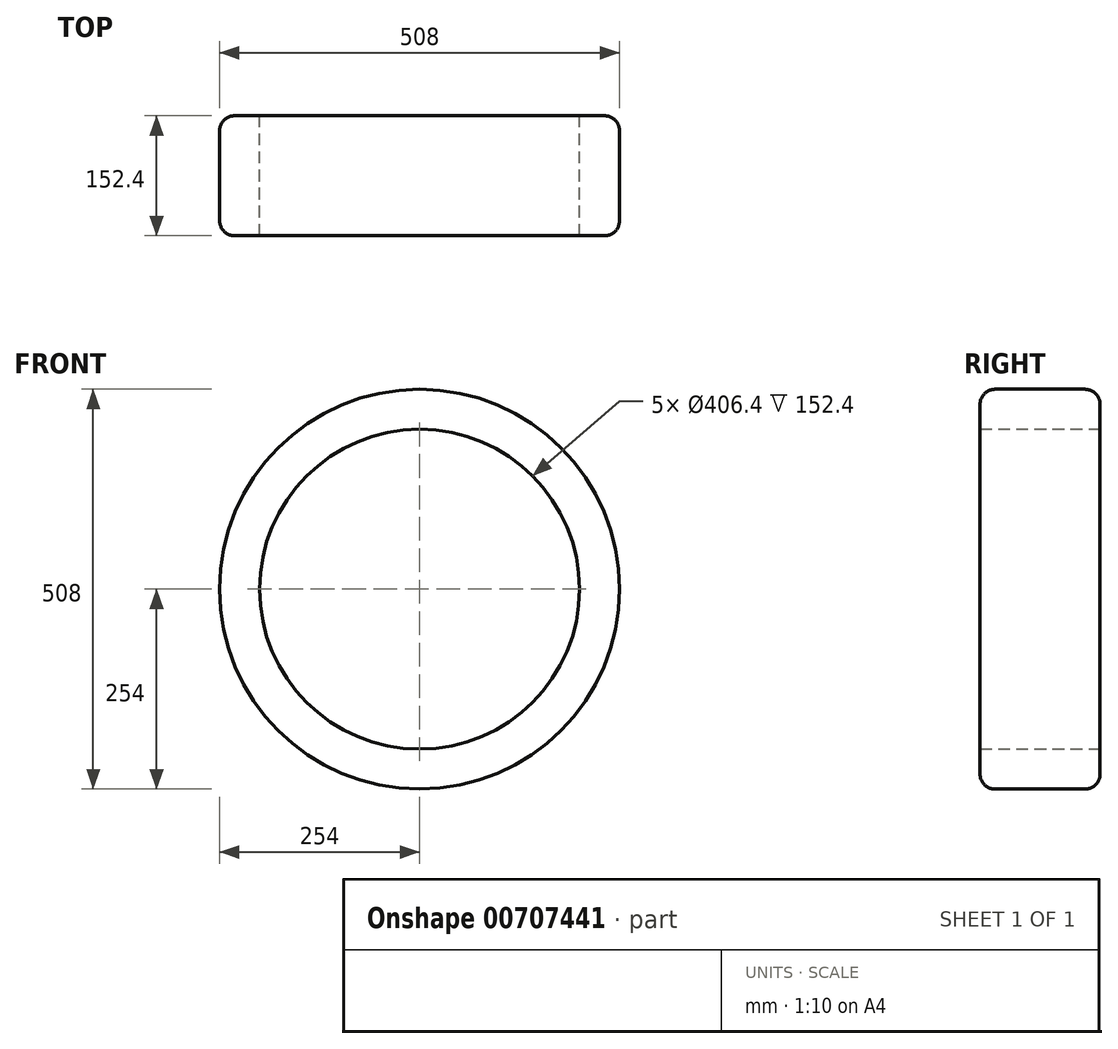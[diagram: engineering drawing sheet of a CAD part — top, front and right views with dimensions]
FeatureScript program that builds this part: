
annotation { "Feature Type Name" : "Feature", "Feature Type Description" : "" }
export const myFeature = defineFeature(function(context is Context, id is Id, definition is map)
    precondition{}
    {
        {
            var Q0;
            Q0=qCreatedBy(makeId("Front.planeOp"),FACE);
            var sketch = newSketch(context, id + "F0", { "sketchPlane" : qUnion([Q0])});
            skCircle(sketch, "E0", {"center": v(0, 0) * mm, "radius": 254 * mm});
            skLineSegment(sketch, "E1", {"start": v(320.36, 0) * mm, "end": v(-315.23, 0) * mm, "construction": true});
            skCircle(sketch, "E2.0", {"center": v(0, 0) * mm, "radius": 203.2 * mm});
            skSolve(sketch);
        }
        {
            var Q0;
            Q0=qCreatedBy(makeId("Top.planeOp"),FACE);
            var sketch = newSketch(context, id + "F1", { "sketchPlane" : qUnion([Q0])});
            skLineSegment(sketch, "E3", {"start": v(0, 100.46) * mm, "end": v(0, -121.76) * mm, "construction": true});
            skSolve(sketch);
        }
        {
            var Q0;
            Q0=makeQuery(id+"F0.imprint","IMPRINT",FACE,{"disambiguationData":[TD([[makeQuery(id+"F0.imprint","IMPRINT",EDGE,{"derivedFrom":sQuery(id+"F0.wireOp",EDGE,"E0")}),1.0]])]});
            extrude(context, id + "F2", {"entities" : qUnion([Q0]), "depth" : 76.2 * mm, "offsetDistance" : 25.4 * mm, "hasSecondDirection" : true, "secondDirectionOppositeDirection" : true, "secondDirectionDepth" : 76.2 * mm});
        }
        {
            var Q0;
            Q0=makeQuery(id+"F2.opExtrude","CAP_EDGE",EDGE,{"disambiguationData":[OSD([sQuery(id+"F0.wireOp",EDGE,"E0")])],"isStart":true});
            var Q1;
            Q1=makeQuery(id+"F2.opExtrude","CAP_EDGE",EDGE,{"disambiguationData":[OSD([sQuery(id+"F0.wireOp",EDGE,"E0")])],"isStart":false});
            fillet(context, id + "F3", {"entities" : qUnion([Q0, Q1]), "radius" : 19.05 * mm, "tangentPropagation" : true, "allowEdgeOverflow" : false});
        }
        {
            var Q0;
            Q0=sQuery(id+"F0.wireOp",EDGE,"E1");
            cPlane(context, id + "F4", {"entities" : qUnion([Q0]), "cplaneType" : CPlaneType.LINE_ANGLE, "offset" : 25.4 * mm, "angle" : 90 * degree, "width" : 152.4 * mm, "height" : 152.4 * mm});
        }
        {
            var Q0;
            Q0=qCreatedBy(id+"F4.planeOp",FACE);
            var sketch = newSketch(context, id + "F5", { "sketchPlane" : qUnion([Q0])});
            skLineSegment(sketch, "E4", {"start": v(234.95, 76.2) * mm, "end": v(234.95, -76.2) * mm});
            skArc(sketch, "E5", {"start": v(234.95, -76.2) * mm, "mid": v(297.42, 0) * mm, "end": v(234.95, 76.2) * mm});
            skSolve(sketch);
        }
        {
            var Q0;
            Q0=sQuery(id+"F5.wireOp",EDGE,"E5");
            var Q1;
            Q1=sQuery(id+"F5.wireOp",EDGE,"E4");
            var Q2;
            Q2=sQuery(id+"F1.wireOp",EDGE,"E3");
            revolve(context, id + "F6", {"bodyType" : ToolBodyType.SURFACE, "surfaceOperationType" : NewSurfaceOperationType.NEW, "surfaceEntities" : qUnion([Q0, Q1]), "axis" : qUnion([Q2]), "revolveType" : RevolveType.FULL});
        }
    });
